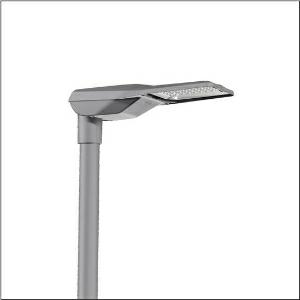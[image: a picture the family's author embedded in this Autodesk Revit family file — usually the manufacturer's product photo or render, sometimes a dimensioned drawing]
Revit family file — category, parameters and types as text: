
# Revit family: streetlight_sl_21_mini___st1_5a_5xe6p43a08gb_223e
name_source: partatom
category: Lighting Fixtures
units: mm (PartAtom-declared; Revit-internal decimal feet)

## family parameters
Cut with Voids When Loaded = No
Host = Face
Light Source = No
Part Type = Normal
Room Calculation Point = No
Round Connector Dimension = Use Diameter
Shared = No

## types (1)
- --- (1 x LED, 6080 lm, 40.4 W, 4000K)
    Apparent Load = 40 VA
    CIE Flux Codes = 22 53 95 100 100
    Color Rendering = 70
    Color Temperature = 4000K
    Default Elevation = 1800 mm
    Description = Streetlight SL 21 mini, mast luminaire, primary light control with lens, of PMMA, primary optical cover: cover, of toughened safety glass, transparent, light distribution: ST1.5a, light emission: direct distribution, primary light characteristic: asymmetric, installation type: post-top, side-entry, LED, 3G 1.5mm², High Power LED, rated luminous flux: 6.080lm, luminous efficacy: 151lm/W, light colour: 740, colour temperature: 4000K, control gear: Easy, control: overheat protection, constant luminous flux control, time-dependent luminous flux control, flexible luminous flux parameterisation, mains connection: 230..240V, AC, 50/60Hz, connection cable pre-assembled, cable length: 6,5m, wiring characteristics: H07RN-F, start of lifetime: 40W, end of service life: 41W, reduction: 19W, luminaire housing, of diecast aluminium, powder-coated, Siteco® metallic grey (DB 702S), corrosivity category C5 mid according to DIN EN ISO 12944, please order mast flange separately, inclination adjustable: 0°, 5°, 10°, 15°, sealing non-destructively replaceable, multi-level sealing system, length: 628mm, width: 235mm, height: 110mm, mast flange for spigot size: 42mm (side-entry): 5XC10008XM4, 60/48mm (side-entry/post-top): 5XC10108XM2, 76/60mm (side-entry/post-top): 5XC10108XM1, mounting height: 4..8m, protection rating (complete): IP66, insulation class (complete): insulation class II (safety insulation), certification: CE, ENEC, ENEC+, VDE, impact resistance: IK10, permissible operating ambient temperature for outdoor applications: -40..+50°C, standard-compliant lighting for roads and squares, packaging unit: 1 piece

Light Distribution: ST1.5a
    Height = 110 mm
    Lamp = 1 x LED
    Lamp Light Flux = 6080 lm
    Lamp Power = 40.4 W
    Lamp count = 1
    Length = 625 mm
    Luminous efficacy = 151 lm/W
    Manufacturer = Siteco
    ModVariant = No
    Model = 5XE6P43A08GB
    Number of Poles = 1
    OnlyDefault = Yes
    Power Factor = 1
    Product Name = Streetlight SL 21 mini | ST1.5a
    Product group = mast luminaire | pylon top
    ProductGroupID = 6100
    Protection Class = Protection class II
    Protection Degree = IP 66
    RLX_Detail_Level = 1
    RLX_Emergency_Light_Flux = 0 lm
    RLX_Emergency_Type = 0
    RLX_Emergency_Type_DB = No
    RlxData = <blob elided: 29453 chars, md5=a02d8999>
    Socket = socket
    Standby Power = 0 W
    System Light Flux = 6080 lm
    System Power = 40 W
    Type Comments = factory setting: luminous flux: 100 % | Output Level: 100 % | 812 mA
    Type Image = l_1003519.jpg
    URL = http://relux.com
    VarID = @adj_175384
    Voltage = 0 V
    Weight = 0.00 kg
    Width = 234 mm

## geometry (parser evidence)
native form markers: Blend x4, Sweep x8
no freeform markers — native parametric forms only
